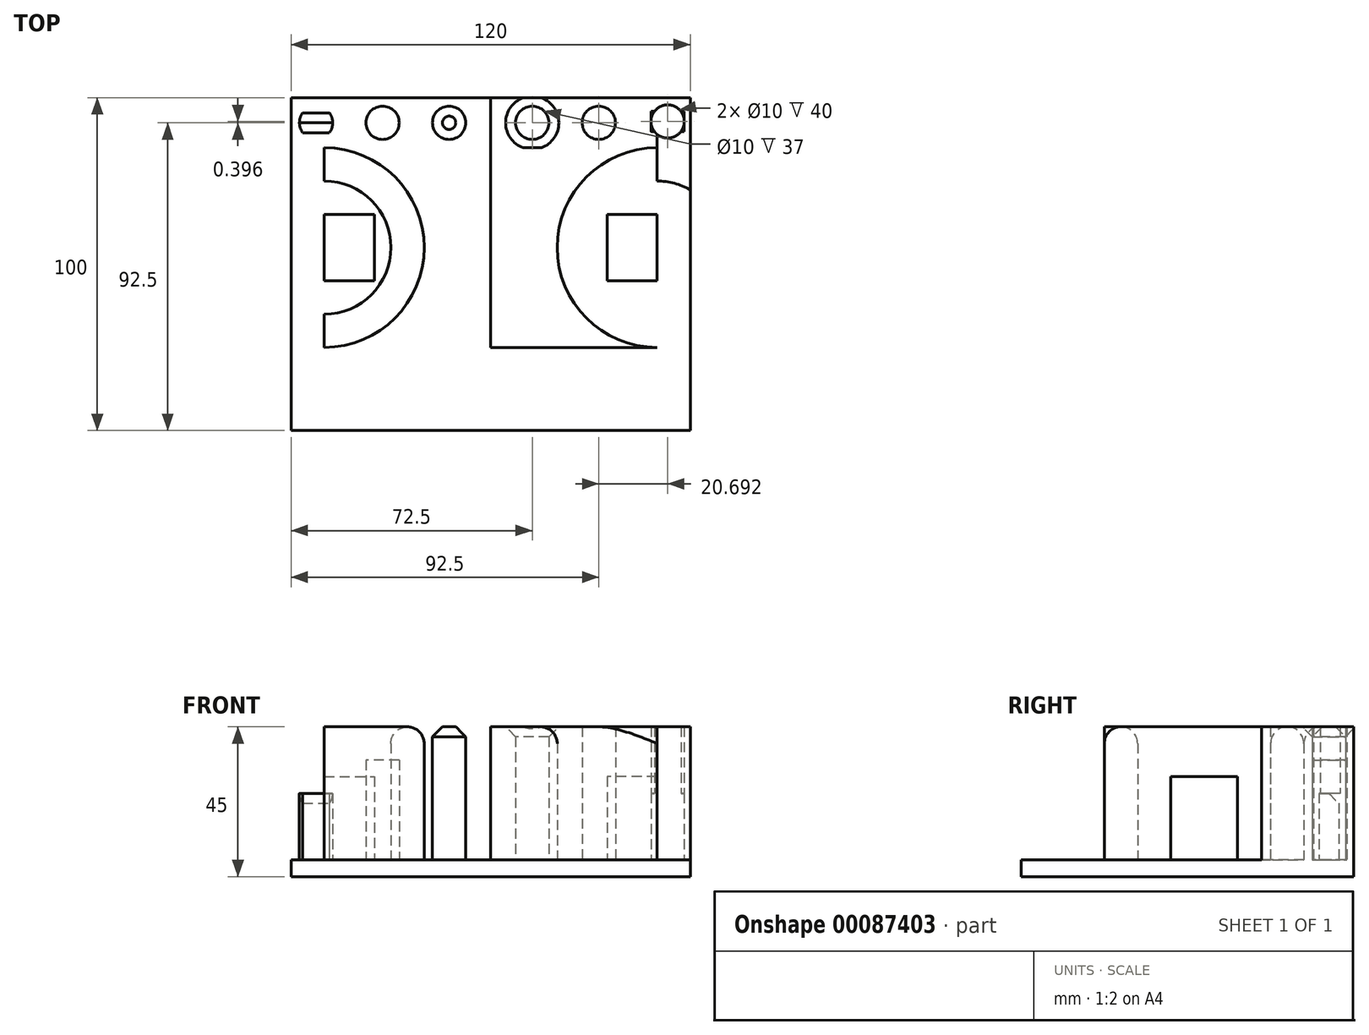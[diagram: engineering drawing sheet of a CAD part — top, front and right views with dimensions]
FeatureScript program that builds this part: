
annotation { "Feature Type Name" : "Feature", "Feature Type Description" : "" }
export const myFeature = defineFeature(function(context is Context, id is Id, definition is map)
    precondition{}
    {
        {
            var Q0;
            Q0=qCreatedBy(makeId("Top.planeOp"),FACE);
            var sketch = newSketch(context, id + "F0", { "sketchPlane" : qUnion([Q0])});
            skLineSegment(sketch, "E0.bottom", {"start": v(-60, 50) * mm, "end": v(60, 50) * mm});
            skLineSegment(sketch, "E0.top", {"start": v(-60, -50) * mm, "end": v(60, -50) * mm});
            skLineSegment(sketch, "E0.left", {"start": v(-60, 50) * mm, "end": v(-60, -50) * mm});
            skLineSegment(sketch, "E0.right", {"start": v(60, 50) * mm, "end": v(60, -50) * mm});
            skPoint(sketch, "E0.middle", {"position": v(0, 0) * mm});
            skSolve(sketch);
        }
        {
            var Q0;
            Q0 = qSketchRegion(id + "F0", true);
            extrude(context, id + "F1", {"entities" : qUnion([Q0]), "depth" : 5 * mm});
        }
        {
            var Q0;
            Q0=makeQuery(id+"F1.opExtrude","CAP_FACE",FACE,{"disambiguationData":[OSD([sQuery(id+"F0.wireOp",EDGE,"E0.bottom"),sQuery(id+"F0.wireOp",EDGE,"E0.top"),sQuery(id+"F0.wireOp",EDGE,"E0.left"),sQuery(id+"F0.wireOp",EDGE,"E0.right")])],"isStart":false});
            var sketch = newSketch(context, id + "F2", { "sketchPlane" : qUnion([Q0])});
            skCircle(sketch, "E1", {"center": v(-52.5, 42.5) * mm, "radius": 5 * mm});
            skCircle(sketch, "E2", {"center": v(-32.5, 42.5) * mm, "radius": 5 * mm});
            skCircle(sketch, "E3", {"center": v(-12.5, 42.5) * mm, "radius": 5 * mm});
            skCircle(sketch, "E4.MirrorC", {"center": v(12.5, 42.5) * mm, "radius": 5 * mm});
            skCircle(sketch, "E5.MirrorC", {"center": v(32.5, 42.5) * mm, "radius": 5 * mm});
            skCircle(sketch, "E6.MirrorC", {"center": v(53.2, 42.9) * mm, "radius": 5 * mm});
            skLineSegment(sketch, "E7.bottom", {"start": v(-57.5, 45.5) * mm, "end": v(-47.5, 45.5) * mm});
            skLineSegment(sketch, "E7.top", {"start": v(-57.5, 39.5) * mm, "end": v(-47.5, 39.5) * mm});
            skLineSegment(sketch, "E7.left", {"start": v(-57.5, 45.5) * mm, "end": v(-57.5, 39.5) * mm});
            skLineSegment(sketch, "E7.right", {"start": v(-47.5, 45.5) * mm, "end": v(-47.5, 39.5) * mm});
            skLineSegment(sketch, "E8.bottom", {"start": v(58.2, 45.9) * mm, "end": v(48.2, 45.9) * mm});
            skLineSegment(sketch, "E8.top", {"start": v(58.2, 39.9) * mm, "end": v(48.2, 39.9) * mm});
            skLineSegment(sketch, "E8.left", {"start": v(58.2, 45.9) * mm, "end": v(58.2, 39.9) * mm});
            skLineSegment(sketch, "E8.right", {"start": v(48.2, 45.9) * mm, "end": v(48.2, 39.9) * mm});
            skLineSegment(sketch, "E9.bottom", {"start": v(-50, 35) * mm, "end": v(50, 35) * mm});
            skPoint(sketch, "E9.middle", {"position": v(0, -2.57) * mm});
            skLineSegment(sketch, "E10.top", {"start": v(-50, -25) * mm, "end": v(50, -25) * mm});
            skLineSegment(sketch, "E10.left", {"start": v(-50, 35) * mm, "end": v(-50, -25) * mm});
            skLineSegment(sketch, "E10.right", {"start": v(50, 35) * mm, "end": v(50, -25) * mm});
            skArc(sketch, "E11", {"start": v(-50, -25) * mm, "mid": v(-20, 5) * mm, "end": v(-50, 35) * mm});
            skLineSegment(sketch, "E12", {"start": v(0, 50) * mm, "end": v(0, -50) * mm});
            skCircle(sketch, "E13", {"center": v(-50, 5) * mm, "radius": 20 * mm});
            skLineSegment(sketch, "E14.bottom", {"start": v(-65, 15) * mm, "end": v(-35, 15) * mm});
            skLineSegment(sketch, "E14.top", {"start": v(-65, -5) * mm, "end": v(-35, -5) * mm});
            skLineSegment(sketch, "E14.left", {"start": v(-65, 15) * mm, "end": v(-65, -5) * mm});
            skLineSegment(sketch, "E14.right", {"start": v(-35, 15) * mm, "end": v(-35, -5) * mm});
            skArc(sketch, "E15.MirrorCS", {"start": v(50, -25) * mm, "mid": v(20, 5) * mm, "end": v(50, 35) * mm});
            skCircle(sketch, "E16.MirrorC", {"center": v(50, 5) * mm, "radius": 20 * mm});
            skLineSegment(sketch, "E17.MirrorCS", {"start": v(35, 15) * mm, "end": v(35, -5) * mm});
            skLineSegment(sketch, "E18.MirrorCS", {"start": v(65, 15) * mm, "end": v(35, 15) * mm});
            skLineSegment(sketch, "E19.MirrorCS", {"start": v(65, -5) * mm, "end": v(35, -5) * mm});
            skSolve(sketch);
        }
        {
            var Q0;
            Q0=makeQuery(id+"F2.imprint","IMPRINT",FACE,{"disambiguationData":[TD([[makeQuery(id+"F2.imprint","IMPRINT",EDGE,{"derivedFrom":sQuery(id+"F2.wireOp",EDGE,"E4.MirrorC")}),-1.0]])]});
            var Q1;
            Q1=makeQuery(id+"F2.imprint","IMPRINT",FACE,{"disambiguationData":[TD([[makeQuery(id+"F2.imprint","IMPRINT",EDGE,{"derivedFrom":sQuery(id+"F2.wireOp",EDGE,"E3")}),1.0]])]});
            extrude(context, id + "F3", {"entities" : qUnion([Q0, Q1]), "operationType" : NewBodyOperationType.ADD, "depth" : 40 * mm});
        }
        {
            var Q0;
            Q0=makeQuery(id+"F2.imprint","IMPRINT",FACE,{"disambiguationData":[TD([[makeQuery(id+"F2.imprint","IMPRINT",EDGE,{"derivedFrom":sQuery(id+"F2.wireOp",EDGE,"E2")}),1.0]])]});
            var Q1;
            Q1=makeQuery(id+"F2.imprint","IMPRINT",FACE,{"disambiguationData":[TD([[makeQuery(id+"F2.imprint","IMPRINT",EDGE,{"derivedFrom":sQuery(id+"F2.wireOp",EDGE,"E5.MirrorC")}),-1.0]])]});
            extrude(context, id + "F4", {"entities" : qUnion([Q0, Q1]), "operationType" : NewBodyOperationType.ADD, "depth" : 30 * mm});
        }
        {
            var Q0;
            Q0=makeQuery(id+"F2.imprint","IMPRINT",FACE,{"disambiguationData":[TD([[makeQuery(id+"F2.imprint","IMPRINT",EDGE,{"derivedFrom":sQuery(id+"F2.wireOp",EDGE,"E1")}),1.0]])]});
            var Q1;
            Q1=makeQuery(id+"F2.imprint","IMPRINT",FACE,{"disambiguationData":[TD([[makeQuery(id+"F2.imprint","IMPRINT",EDGE,{"derivedFrom":sQuery(id+"F2.wireOp",EDGE,"E6.MirrorC")}),-1.0]])]});
            extrude(context, id + "F5", {"entities" : qUnion([Q0, Q1]), "operationType" : NewBodyOperationType.ADD, "depth" : 20 * mm});
        }
        {
            var Q0;
            Q0=makeQuery(id+"F3.opExtrude","CAP_EDGE",EDGE,{"disambiguationData":[OSD([sQuery(id+"F2.wireOp",EDGE,"E3")])],"isStart":false});
            var Q1;
            Q1=makeQuery(id+"F3.opExtrude","CAP_EDGE",EDGE,{"disambiguationData":[OSD([sQuery(id+"F2.wireOp",EDGE,"E4.MirrorC")])],"isStart":false});
            chamfer(context, id + "F6", {"entities" : qUnion([Q0, Q1]), "width" : 3 * mm, "tangentPropagation" : true});
        }
        {
            var Q0;
            Q0=makeQuery(id+"F5.opExtrude","CAP_EDGE",EDGE,{"disambiguationData":[OSD([sQuery(id+"F2.wireOp",EDGE,"E7.bottom")])],"isStart":false});
            var Q1;
            Q1=makeQuery(id+"F5.opExtrude","CAP_EDGE",EDGE,{"disambiguationData":[OSD([sQuery(id+"F2.wireOp",EDGE,"E8.bottom")])],"isStart":false});
            chamfer(context, id + "F7", {"entities" : qUnion([Q0, Q1]), "width" : 3 * mm, "tangentPropagation" : true});
        }
        {
            var Q0;
            {var subQ0=sQuery(id+"F2.wireOp",EDGE,"E11");Q0=makeQuery(id+"F2.imprint","IMPRINT",FACE,{"disambiguationData":[TD([[makeQuery(id+"F2.imprint","IMPRINT",EDGE,{"derivedFrom":subQ0}),1.0]])]});}
            var Q1;
            {var subQ0=sQuery(id+"F2.wireOp",EDGE,"E15.MirrorCS");Q1=makeQuery(id+"F2.imprint","IMPRINT",FACE,{"disambiguationData":[TD([[makeQuery(id+"F2.imprint","IMPRINT",EDGE,{"derivedFrom":subQ0}),-1.0]])]});}
            extrude(context, id + "F8", {"entities" : qUnion([Q0, Q1]), "operationType" : NewBodyOperationType.ADD, "depth" : 40 * mm});
        }
        {
            var Q0;
            {var subQ5=sQuery(id+"F2.wireOp",EDGE,"E14.right");Q0=makeQuery(id+"F2.imprint","IMPRINT",FACE,{"disambiguationData":[TD([[makeQuery(id+"F2.imprint","IMPRINT",EDGE,{"derivedFrom":subQ5}),-1.0]])]});}
            var Q1;
            {var subQ5=sQuery(id+"F2.wireOp",EDGE,"E17.MirrorCS");Q1=makeQuery(id+"F2.imprint","IMPRINT",FACE,{"disambiguationData":[TD([[makeQuery(id+"F2.imprint","IMPRINT",EDGE,{"derivedFrom":subQ5}),1.0]])]});}
            extrude(context, id + "F9", {"entities" : qUnion([Q0, Q1]), "operationType" : NewBodyOperationType.ADD, "depth" : 25 * mm});
        }
        {
            var Q0;
            Q0=makeQuery(id+"F8.opExtrude","CAP_EDGE",EDGE,{"disambiguationData":[OSD([sQuery(id+"F2.wireOp",EDGE,"E16.MirrorC")])],"isStart":false});
            var Q1;
            Q1=makeQuery(id+"F8.opExtrude","CAP_EDGE",EDGE,{"disambiguationData":[OSD([sQuery(id+"F2.wireOp",EDGE,"E13")])],"isStart":false});
            var Q2;
            Q2=makeQuery(id+"F8.opExtrude","CAP_EDGE",EDGE,{"disambiguationData":[OSD([sQuery(id+"F2.wireOp",EDGE,"E11")])],"isStart":false});
            var Q3;
            Q3=makeQuery(id+"F8.opExtrude","CAP_EDGE",EDGE,{"disambiguationData":[OSD([sQuery(id+"F2.wireOp",EDGE,"E15.MirrorCS")])],"isStart":false});
            var Q4;
            {var subQ0=sQuery(id+"F2.wireOp",EDGE,"E10.left");Q4=makeQuery(id+"F8.opExtrude","SWEPT_FACE",FACE,{"disambiguationData":[OSD([subQ0]),TDD([makeQuery(id+"F2.imprint","IMPRINT",EDGE,{"disambiguationData":[TD([[makeQuery(id+"F2.imprint","INTERSECT",VERTEX,{"disambiguationData":[OD(1.0)],"derivedFrom":[subQ0,sQuery(id+"F2.wireOp",EDGE,"E13")]}),-1.0]])],"derivedFrom":subQ0})])]});}
            var Q5;
            {var subQ0=sQuery(id+"F2.wireOp",EDGE,"E10.left");Q5=makeQuery(id+"F8.opExtrude","SWEPT_FACE",FACE,{"disambiguationData":[OSD([subQ0]),TDD([makeQuery(id+"F2.imprint","IMPRINT",EDGE,{"disambiguationData":[TD([[makeQuery(id+"F2.imprint","INTERSECT",VERTEX,{"disambiguationData":[OD(0.0)],"derivedFrom":[subQ0,sQuery(id+"F2.wireOp",EDGE,"E13")]}),1.0]])],"derivedFrom":subQ0})])]});}
            var Q6;
            {var subQ0=sQuery(id+"F2.wireOp",EDGE,"E10.right");Q6=makeQuery(id+"F8.opExtrude","SWEPT_FACE",FACE,{"disambiguationData":[OSD([subQ0]),TDD([makeQuery(id+"F2.imprint","IMPRINT",EDGE,{"disambiguationData":[TD([[makeQuery(id+"F2.imprint","INTERSECT",VERTEX,{"disambiguationData":[OD(1.0)],"derivedFrom":[subQ0,sQuery(id+"F2.wireOp",EDGE,"E16.MirrorC")]}),-1.0]])],"derivedFrom":subQ0})])]});}
            var Q7;
            {var subQ0=sQuery(id+"F2.wireOp",EDGE,"E10.right");Q7=makeQuery(id+"F8.opExtrude","SWEPT_FACE",FACE,{"disambiguationData":[OSD([subQ0]),TDD([makeQuery(id+"F2.imprint","IMPRINT",EDGE,{"disambiguationData":[TD([[makeQuery(id+"F2.imprint","INTERSECT",VERTEX,{"disambiguationData":[OD(0.0)],"derivedFrom":[subQ0,sQuery(id+"F2.wireOp",EDGE,"E16.MirrorC")]}),1.0]])],"derivedFrom":subQ0})])]});}
            fillet(context, id + "F10", {"entities" : qUnion([Q0, Q1, Q2, Q3, Q4, Q5, Q6, Q7]), "radius" : 5 * mm, "tangentPropagation" : true, "allowEdgeOverflow" : false});
        }
    });
